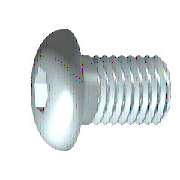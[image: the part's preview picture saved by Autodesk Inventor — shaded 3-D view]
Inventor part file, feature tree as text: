
AUTODESK INVENTOR PART (.ipt)
format: ipt  version: 2023.4 (Build 274418000, 418)  size: 205,312 bytes
history: native  units: mm (DEFAULTED — no unit token found)
features: extrude x1, plane x1, fillet x1
ambient origin geometry x7: Origin, YZ Plane, XY Plane, X Axis, Y Axis, Z Axis, Center Point
bodies: Solid1 (feature_tree), Body (feature_tree)
feature tree (3):
  extrude  "Slot"  Depth=1.0666mm
  plane  "Work Plane1"
  fillet  "Fillet2"  Radius=2.1083mm
